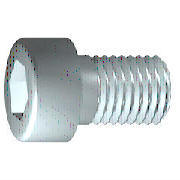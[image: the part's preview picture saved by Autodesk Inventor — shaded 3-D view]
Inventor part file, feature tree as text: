
AUTODESK INVENTOR PART (.ipt)
format: ipt  version: 2016 (Build 200138000, 138)  size: 192,000 bytes
history: native  units: mm (DEFAULTED — no unit token found)
features: sketch x2, other x1, extrude x1, plane x1, fillet x1
ambient origin geometry x7: Origin, YZ Plane, XY Plane, X Axis, Y Axis, Z Axis, Center Point
bodies: Solid1 (feature_tree)
feature tree (6):
  other  "Körper"
  extrude  "Loch"  Depth=3.0mm
  plane  "Work Plane1"
  fillet  "Fillet2"  Radius=3.0mm
  sketch  "Skizze1"  dims[d1=8.75mm d2=0.306825mm d3=3.0mm]
  sketch  "Skizze2"  dims[d4=1.3mm d5=60.0deg d6=3.0mm d7=3.0mm d8=2.886751mm d9=5.5mm d10=90.0deg d11=10.0mm d12=0.0mm d13=8.75mm d14=0.0mm d15=0.306725mm d16=0.306725mm d17=0.3mm d19=0.0mm d26=10.0mm d27=45.0deg d28=0.0mm d29=0.0mm d30=0.1mm]
